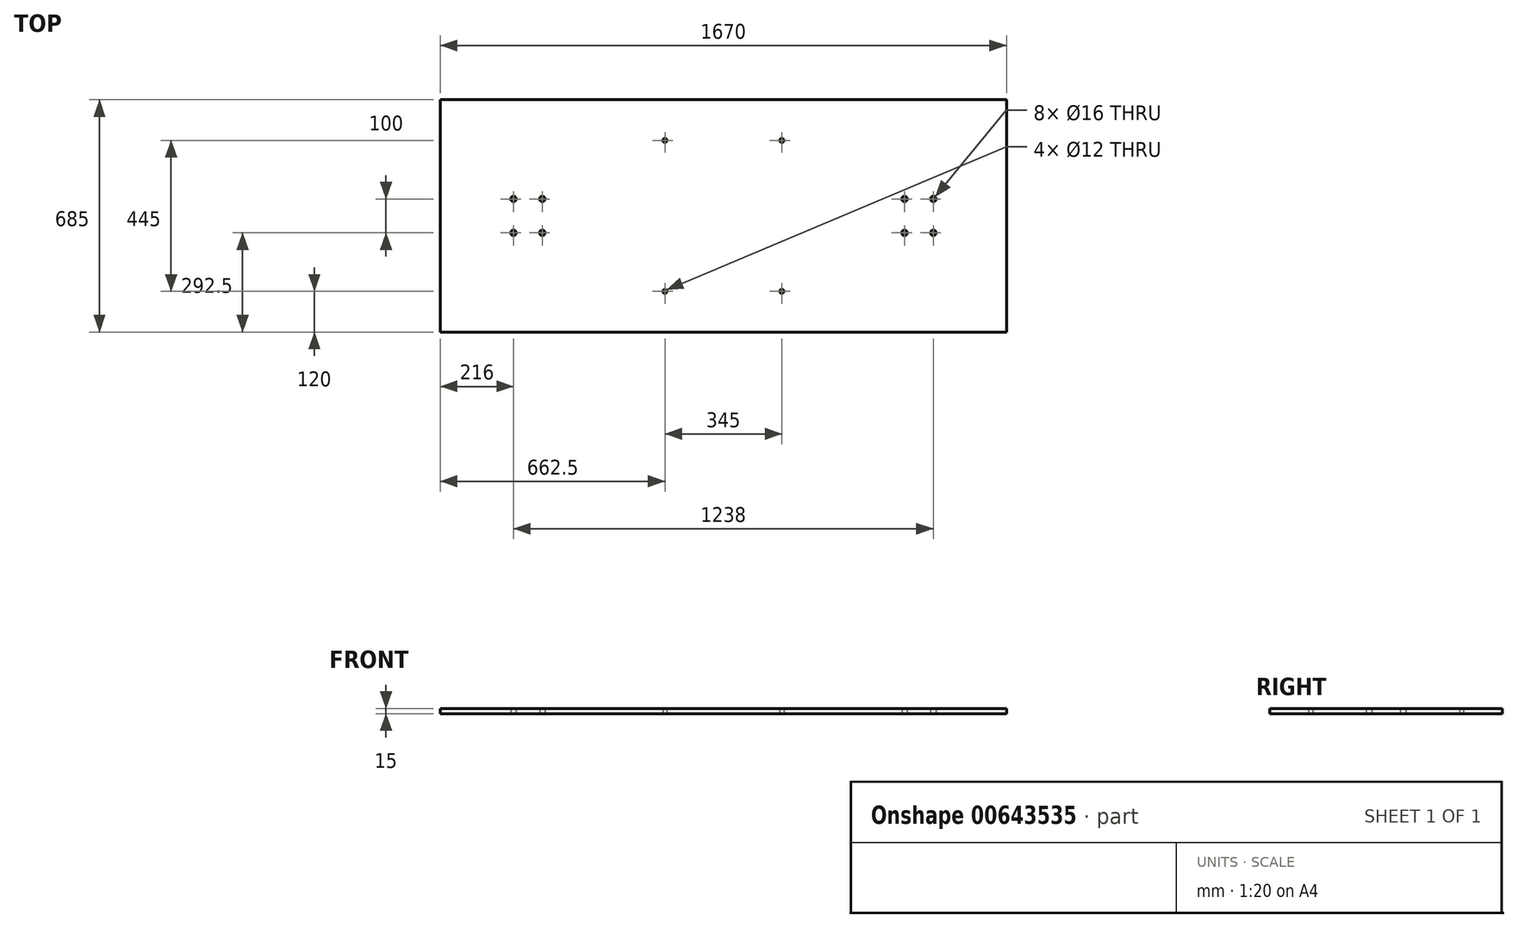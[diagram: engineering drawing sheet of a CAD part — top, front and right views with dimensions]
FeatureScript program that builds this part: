
annotation { "Feature Type Name" : "Feature", "Feature Type Description" : "" }
export const myFeature = defineFeature(function(context is Context, id is Id, definition is map)
    precondition{}
    {
        {
            var Q0;
            Q0=qCreatedBy(makeId("Top.planeOp"),FACE);
            var sketch = newSketch(context, id + "F0", { "sketchPlane" : qUnion([Q0])});
            skLineSegment(sketch, "E0.bottom", {"start": v(-835, -342.5) * mm, "end": v(835, -342.5) * mm});
            skLineSegment(sketch, "E0.top", {"start": v(-835, 342.5) * mm, "end": v(835, 342.5) * mm});
            skLineSegment(sketch, "E0.left", {"start": v(-835, -342.5) * mm, "end": v(-835, 342.5) * mm});
            skLineSegment(sketch, "E0.right", {"start": v(835, -342.5) * mm, "end": v(835, 342.5) * mm});
            skPoint(sketch, "E0.middle", {"position": v(0, 0) * mm});
            skLineSegment(sketch, "E1", {"start": v(-835, 0) * mm, "end": v(835, 0) * mm, "construction": true});
            skLineSegment(sketch, "E2", {"start": v(0, 342.5) * mm, "end": v(0, -342.5) * mm, "construction": true});
            skCircle(sketch, "E3", {"center": v(-619, 50) * mm, "radius": 8 * mm});
            skCircle(sketch, "E4", {"center": v(-172.5, 222.5) * mm, "radius": 6 * mm});
            skCircle(sketch, "E5.MirrorC", {"center": v(619, 50) * mm, "radius": 8 * mm});
            skCircle(sketch, "E6.MirrorC", {"center": v(172.5, 222.5) * mm, "radius": 6 * mm});
            skCircle(sketch, "E7.MirrorC", {"center": v(619, -50) * mm, "radius": 8 * mm});
            skCircle(sketch, "E8.MirrorC", {"center": v(172.5, -222.5) * mm, "radius": 6 * mm});
            skCircle(sketch, "E9.MirrorC", {"center": v(-172.5, -222.5) * mm, "radius": 6 * mm});
            skCircle(sketch, "E10.MirrorC", {"center": v(-619, -50) * mm, "radius": 8 * mm});
            skCircle(sketch, "E11", {"center": v(-534, 50) * mm, "radius": 8 * mm});
            skCircle(sketch, "E12.MirrorC", {"center": v(534, 50) * mm, "radius": 8 * mm});
            skCircle(sketch, "E13.MirrorC", {"center": v(-534, -50) * mm, "radius": 8 * mm});
            skCircle(sketch, "E14.MirrorC", {"center": v(534, -50) * mm, "radius": 8 * mm});
            skSolve(sketch);
        }
        {
            var Q0;
            Q0 = qSketchRegion(id + "F0", true);
            extrude(context, id + "F1", {"entities" : qUnion([Q0]), "depth" : 15 * mm, "offsetDistance" : 25 * mm});
        }
    });
